# Revit family: Fallrohrstütze DN125 u. DN150-Set
name_source: partatom
category: HLS-Bauteile
revit_build: Autodesk Revit 2017 (Build: 20190507_1515(x64)
units: mm (PartAtom-declared; Revit-internal decimal feet)

## family parameters
Basisbauteil = Fläche
Beim Laden mit Abzugskörper schneiden = Nein
Bemaßung runder Anschluss = Durchmesser verwenden
Gemeinsam genutzt = Ja
Raumberechnungspunkt = Nein
Teiletyp = Normal

## types (2) — shared parameters
6kt.Flanschmutter = Sechskantmutter : Sechskantmutter M10
6kt.Schraube = 6kt.Schraube DIN EN ISO 4017 : M10x 20 SW17
Abstandswinkel = MEFA Abstandswinkel E : MEFA Abstandswinkel E  L= 25
Abstandswinkeltyp = MEFA Abstandswinkel einfach 42x35x4
Baustoffklasse = B2
Fabrikat = MEFA
Farbe Schalldämmeinlage = Schwarz
Firma = MEFA Befestigungs- und Montagesysteme GmbH
Gewindeplattentyp = M10 35x30
Konsole = Konsole 35-42 : Konsole 35/42/1.5,  L=300mm
Konsolentyp = Stex 35/42
Kurztext1 = Fallrohrstützenbefestigung Set SML
Langloch = 15x11 mm
Lochabstand = 80 mm
Länge Konsole = 300 mm
Material = Stahl
Materialname C-Profil = S235JR
Materialname Platte = S235JR
Mengeneinheit = St
Rohrschellentyp = Maxima PSM
Schalldämmeinlage = Gummi
Stärke Material Schalldämmeinlage = 6 mm
Vorgabe-Ansicht = 1219 mm
WA max. = 270 mm  [stored 0.885827 ft]
max. Temperaturbeständigkeit = 100 °C
max. Wandabstand = 300 mm
max. zul. Last F1 = 0.94 kip
max. zul. Last F2 = 0.47 kip
vpe = 1 St

## per-type parameters (varying)
| type | Abstandsmaß | Artikelnummer | B | EAN | Gewicht | Gewicht pro Bauteil | Kurztext2 | Nennweite DN Rohr | Rohraußendurchmesser | Rohrschelle | Setztiefe | min. Wandabstand |
| Fallrohrstütze DN125 | 200 mm | 4501250 | 190 mm | 4250928439550 | 2.68 kg | 2.68 kg | DN 125 / 135 mm Wandabstand 85 - 300 mm | 125 mm  [stored 0.410105 ft] | 135 mm  [stored 0.442913 ft] | MEFA RS Maxima PSM, AG M10-M12, Ø120-Ø275 mm, TPE : MEFA RS Maxima PSM, AG M10-M12, Ø133-Ø136 mm, TPE |  | 85 mm |
| Fallrohrstütze DN150 | 230 mm | 4501500 | 218 mm  [stored 0.715223 ft] | 4250928439567 | 2.79 kg | 2.79 kg | DN 150 / 160 mm Wandabstand 100 - 300 mm | 150 mm | 160 mm  [stored 0.524934 ft] | MEFA RS Maxima PSM, AG M10-M12, Ø120-Ø275 mm, TPE : MEFA RS Maxima PSM, AG M10-M12, Ø158-Ø163 mm, TPE | M10x20 | 100 mm |

note: [stored X ft] marks values corroborated as IEEE doubles in the binary element streams (Revit-internal decimal feet)

## geometry (parser evidence)
native form markers: Sweep x9
no freeform markers — native parametric forms only
